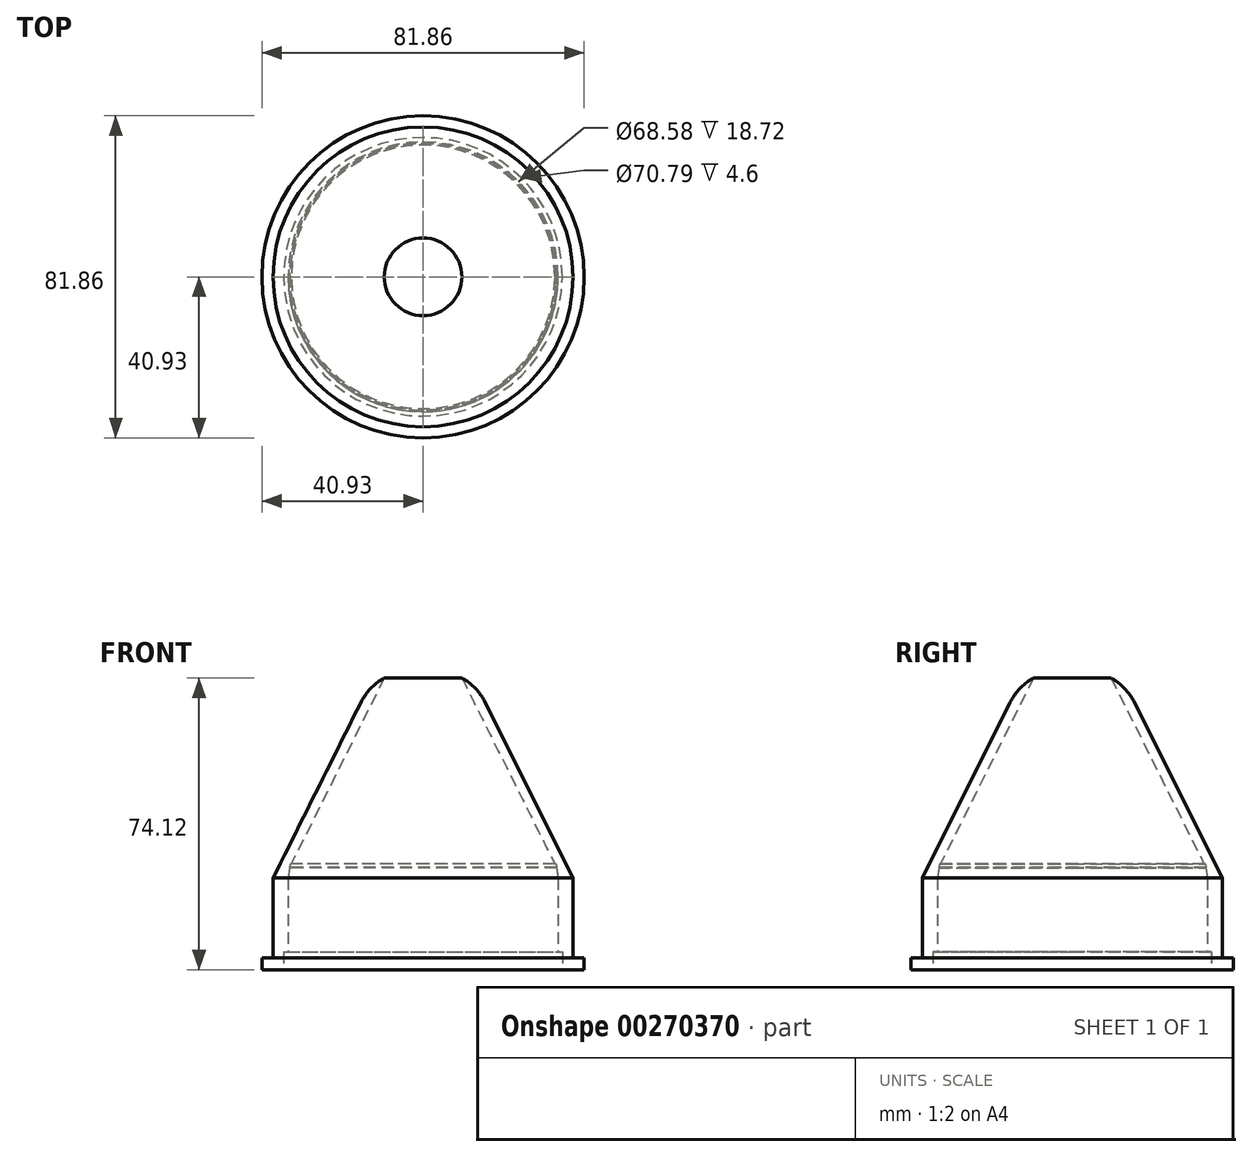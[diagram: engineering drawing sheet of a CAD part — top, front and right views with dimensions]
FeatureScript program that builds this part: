
annotation { "Feature Type Name" : "Feature", "Feature Type Description" : "" }
export const myFeature = defineFeature(function(context is Context, id is Id, definition is map)
    precondition{}
    {
        {
            var Q0;
            Q0=qCreatedBy(makeId("Top.planeOp"),FACE);
            var sketch = newSketch(context, id + "F0", { "sketchPlane" : qUnion([Q0])});
            skCircle(sketch, "E0", {"center": v(0, 0) * mm, "radius": 38.1 * mm});
            skCircle(sketch, "E1", {"center": v(0, 0) * mm, "radius": 34.3 * mm});
            skSolve(sketch);
        }
        {
            var Q0;
            Q0 = qSketchRegion(id + "F0", true);
            extrude(context, id + "F1", {"entities" : qUnion([Q0]), "depth" : 20.32 * mm});
        }
        {
            var Q0;
            Q0=qCreatedBy(makeId("Top.planeOp"),FACE);
            var Q1;
            Q1 = qBodyType(qCreatedBy(id + "F3" ,EDGE), BodyType.WIRE);
            cPlane(context, id + "F2", {"entities" : qUnion([Q0, Q1]), "cplaneType" : CPlaneType.OFFSET, "offset" : 71.12 * mm, "width" : 152.4 * mm, "height" : 152.4 * mm});
        }
        {
            var Q0;
            Q0=qCreatedBy(id+"F2.planeOp",FACE);
            var sketch = newSketch(context, id + "F3", { "sketchPlane" : qUnion([Q0])});
            skCircle(sketch, "E2", {"center": v(0, 0) * mm, "radius": 12.7 * mm});
            skSolve(sketch);
        }
        {
            var Q0;
            Q0=makeQuery(id+"F1.opExtrude","CAP_FACE",FACE,{"disambiguationData":[OSD([sQuery(id+"F0.wireOp",EDGE,"E0"),sQuery(id+"F0.wireOp",EDGE,"E1")])],"isStart":false});
            var sketch = newSketch(context, id + "F4", { "sketchPlane" : qUnion([Q0])});
            skCircle(sketch, "E3.0", {"center": v(0, 0) * mm, "radius": 38.1 * mm});
            skSolve(sketch);
        }
        {
            var Q1;
            Q1 = qSketchRegion(id + "F4", true);
            var Q2;
            Q2 = qSketchRegion(id + "F3", true);
            loft(context, id + "F5", {"operationType" : NewBodyOperationType.ADD, "sheetProfilesArray" : [{ "sheetProfileEntities" : qUnion([Q1]) }, { "sheetProfileEntities" : qUnion([Q2]) }]});
        }
        {
            var Q0;
            Q0=makeQuery(id+"F5.opLoft","CAP_FACE",FACE,{"disambiguationData":[OSD([makeQuery(id+"F3.imprint","IMPRINT",FACE,{"disambiguationData":[TD([[makeQuery(id+"F3.imprint","IMPRINT",EDGE,{"derivedFrom":sQuery(id+"F3.wireOp",EDGE,"E2")}),1.0]])]})])],"isStart":true});
            shell(context, id + "F6", {"entities" : qUnion([Q0]), "thickness" : 2.54 * mm});
        }
        {
            var Q0;
            Q0=makeQuery(id+"F5.opLoft","CAP_FACE",FACE,{"disambiguationData":[OSD([makeQuery(id+"F4.imprint","IMPRINT",FACE,{"disambiguationData":[TD([[makeQuery(id+"F4.imprint","IMPRINT",EDGE,{"derivedFrom":makeQuery(id+"F1.opExtrude","CAP_EDGE",EDGE,{"disambiguationData":[OSD([sQuery(id+"F0.wireOp",EDGE,"E1")])],"isStart":false})}),1.0]])]})])],"isStart":true});
            extrude(context, id + "F7", {"entities" : qUnion([Q0]), "operationType" : NewBodyOperationType.REMOVE, "oppositeDirection" : true, "depth" : 3.56 * mm, "hasDraft" : true, "draftAngle" : 8 * degree, "draftPullDirection" : true});
        }
        {
            var Q0;
            Q0=makeQuery(id+"F5.opLoft","MID_CAP_EDGE",EDGE,{"disambiguationData":[OSD([sQuery(id+"F3.wireOp",EDGE,"E2"),sQuery(id+"F4.wireOp",EDGE,"E3.0")])],"capPos":1.0});
            fillet(context, id + "F8", {"entities" : qUnion([Q0]), "radius" : 14.47 * mm, "tangentPropagation" : true, "allowEdgeOverflow" : false});
        }
        {
            var Q0;
            Q0=qCreatedBy(makeId("Top.planeOp"),FACE);
            var sketch = newSketch(context, id + "F9", { "sketchPlane" : qUnion([Q0])});
            skCircle(sketch, "E4", {"center": v(0, 0) * mm, "radius": 40.93 * mm});
            skSolve(sketch);
        }
        {
            var Q0;
            Q0=makeQuery(id+"F9.imprint","IMPRINT",FACE,{"disambiguationData":[TD([[makeQuery(id+"F9.imprint","IMPRINT",EDGE,{"derivedFrom":sQuery(id+"F9.wireOp",EDGE,"E4")}),1.0]])]});
            extrude(context, id + "F10", {"entities" : qUnion([Q0]), "operationType" : NewBodyOperationType.ADD, "oppositeDirection" : true, "depth" : 3 * mm});
        }
        {
            var Q0;
            Q0=makeQuery(id+"F10.opExtrude","CAP_FACE",FACE,{"disambiguationData":[OSD([sQuery(id+"F9.wireOp",EDGE,"E4")])],"isStart":false});
            var sketch = newSketch(context, id + "F11", { "sketchPlane" : qUnion([Q0])});
            skCircle(sketch, "E5.0", {"center": v(0, 0) * mm, "radius": 35.4 * mm});
            skSolve(sketch);
        }
        {
            var Q0;
            Q0=makeQuery(id+"F11.imprint","IMPRINT",FACE,{"disambiguationData":[TD([[makeQuery(id+"F11.imprint","IMPRINT",EDGE,{"derivedFrom":sQuery(id+"F11.wireOp",EDGE,"E5.0")}),1.0]])]});
            extrude(context, id + "F12", {"entities" : qUnion([Q0]), "operationType" : NewBodyOperationType.REMOVE, "oppositeDirection" : true, "depth" : 4.6 * mm});
        }
    });
